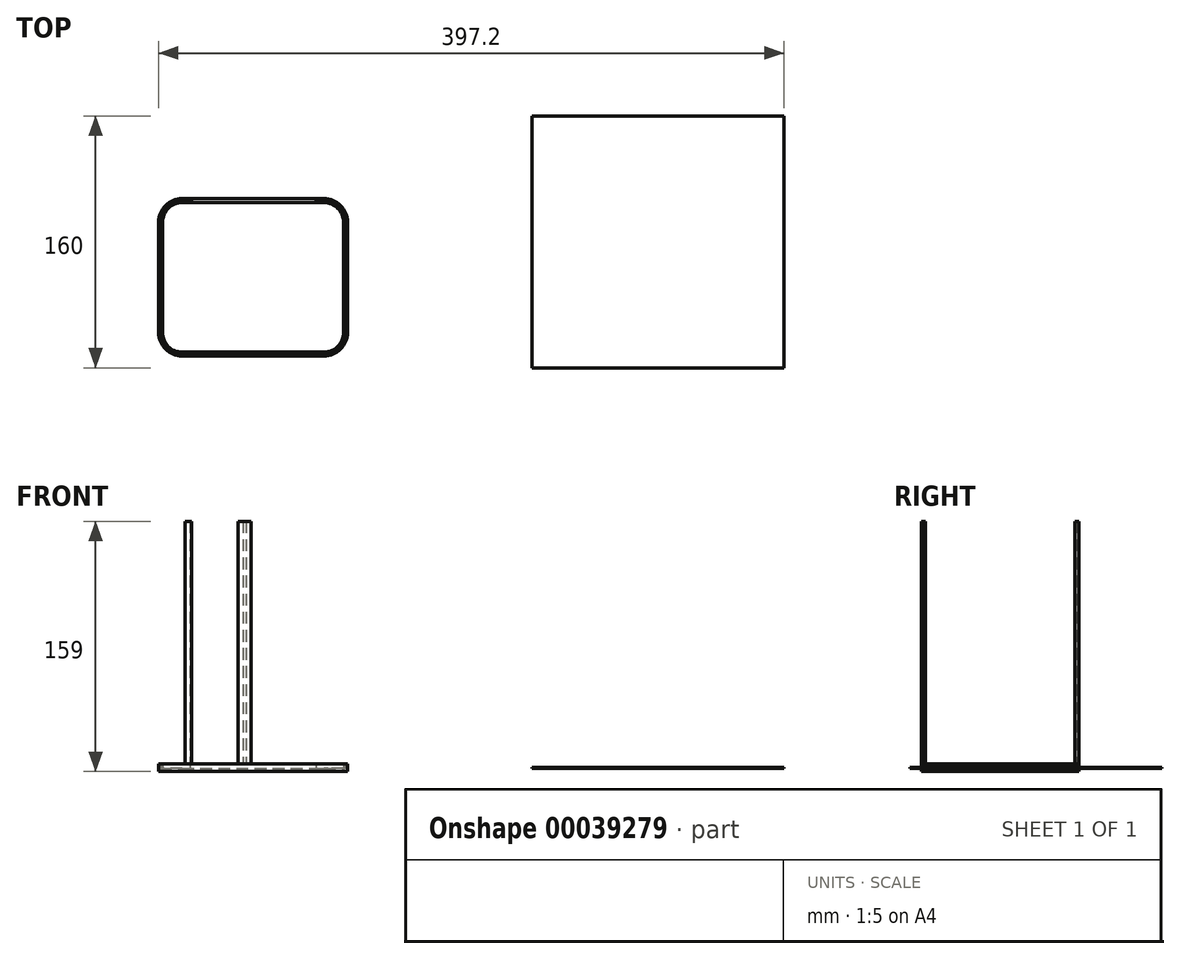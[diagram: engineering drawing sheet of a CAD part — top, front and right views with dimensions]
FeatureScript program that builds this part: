
annotation { "Feature Type Name" : "Feature", "Feature Type Description" : "" }
export const myFeature = defineFeature(function(context is Context, id is Id, definition is map)
    precondition{}
    {
        {
            var Q0;
            Q0=qCreatedBy(makeId("Top.planeOp"),FACE);
            var sketch = newSketch(context, id + "F0", { "sketchPlane" : qUnion([Q0])});
            skLineSegment(sketch, "E0.bottom", {"start": v(0, 0) * mm, "end": v(90, 0) * mm});
            skLineSegment(sketch, "E0.top", {"start": v(0, -100) * mm, "end": v(90, -100) * mm});
            skLineSegment(sketch, "E0.left", {"start": v(-15, -15) * mm, "end": v(-15, -85) * mm});
            skLineSegment(sketch, "E0.right", {"start": v(105, -15) * mm, "end": v(105, -85) * mm});
            skPoint(sketch, "E1.visualSharp", {"position": v(-15, -100) * mm});
            skArc(sketch, "E1.filletArc", {"start": v(-15, -85) * mm, "mid": v(-10.6, -95.6) * mm, "end": v(0, -100) * mm});
            skPoint(sketch, "E2.visualSharp", {"position": v(105, -100) * mm});
            skArc(sketch, "E2.filletArc", {"start": v(90, -100) * mm, "mid": v(100.6, -95.6) * mm, "end": v(105, -85) * mm});
            skPoint(sketch, "E3.visualSharp", {"position": v(105, 0) * mm});
            skArc(sketch, "E3.filletArc", {"start": v(105, -15) * mm, "mid": v(100.6, -4.4) * mm, "end": v(90, 0) * mm});
            skPoint(sketch, "E4.visualSharp", {"position": v(-15, 0) * mm});
            skArc(sketch, "E4.filletArc", {"start": v(0, 0) * mm, "mid": v(-10.6, -4.4) * mm, "end": v(-15, -15) * mm});
            skArc(sketch, "E5.0", {"start": v(0, -2.5) * mm, "mid": v(-8.84, -6.16) * mm, "end": v(-12.5, -15) * mm});
            skLineSegment(sketch, "E5.1", {"start": v(-12.5, -15) * mm, "end": v(-12.5, -85) * mm});
            skLineSegment(sketch, "E5.2", {"start": v(0, -2.5) * mm, "end": v(90, -2.5) * mm});
            skArc(sketch, "E5.3", {"start": v(-12.5, -85) * mm, "mid": v(-8.84, -93.84) * mm, "end": v(0, -97.5) * mm});
            skArc(sketch, "E5.4", {"start": v(102.5, -15) * mm, "mid": v(98.84, -6.16) * mm, "end": v(90, -2.5) * mm});
            skLineSegment(sketch, "E5.5", {"start": v(102.5, -15) * mm, "end": v(102.5, -85) * mm});
            skArc(sketch, "E5.6", {"start": v(90, -97.5) * mm, "mid": v(98.84, -93.84) * mm, "end": v(102.5, -85) * mm});
            skLineSegment(sketch, "E5.7", {"start": v(0, -97.5) * mm, "end": v(90, -97.5) * mm});
            skLineSegment(sketch, "E6.0", {"start": v(0, -0.75) * mm, "end": v(90, -0.75) * mm});
            skArc(sketch, "E6.1", {"start": v(104.25, -15) * mm, "mid": v(100.08, -4.92) * mm, "end": v(90, -0.75) * mm});
            skArc(sketch, "E6.2", {"start": v(0, -0.75) * mm, "mid": v(-10.08, -4.92) * mm, "end": v(-14.25, -15) * mm});
            skLineSegment(sketch, "E6.3", {"start": v(104.25, -15) * mm, "end": v(104.25, -85) * mm});
            skLineSegment(sketch, "E6.4", {"start": v(-14.25, -15) * mm, "end": v(-14.25, -85) * mm});
            skArc(sketch, "E6.5", {"start": v(-14.25, -85) * mm, "mid": v(-10.08, -95.08) * mm, "end": v(0, -99.25) * mm});
            skLineSegment(sketch, "E6.6", {"start": v(0, -99.25) * mm, "end": v(90, -99.25) * mm});
            skArc(sketch, "E6.7", {"start": v(90, -99.25) * mm, "mid": v(100.08, -95.08) * mm, "end": v(104.25, -85) * mm});
            skArc(sketch, "E7.0", {"start": v(0, -1.75) * mm, "mid": v(-9.37, -5.63) * mm, "end": v(-13.25, -15) * mm});
            skLineSegment(sketch, "E7.1", {"start": v(0, -1.75) * mm, "end": v(90, -1.75) * mm});
            skLineSegment(sketch, "E7.2", {"start": v(-13.25, -15) * mm, "end": v(-13.25, -85) * mm});
            skArc(sketch, "E7.3", {"start": v(103.25, -15) * mm, "mid": v(99.37, -5.63) * mm, "end": v(90, -1.75) * mm});
            skArc(sketch, "E7.4", {"start": v(-13.25, -85) * mm, "mid": v(-9.37, -94.37) * mm, "end": v(0, -98.25) * mm});
            skLineSegment(sketch, "E7.5", {"start": v(0, -98.25) * mm, "end": v(90, -98.25) * mm});
            skArc(sketch, "E7.6", {"start": v(90, -98.25) * mm, "mid": v(99.37, -94.37) * mm, "end": v(103.25, -85) * mm});
            skLineSegment(sketch, "E7.7", {"start": v(103.25, -15) * mm, "end": v(103.25, -85) * mm});
            skLineSegment(sketch, "E8", {"start": v(5, 0) * mm, "end": v(5, -2.5) * mm});
            skLineSegment(sketch, "E9", {"start": v(85, 0) * mm, "end": v(85, -2.5) * mm});
            skSolve(sketch);
        }
        {
            var Q0;
            Q0=makeQuery(id+"F0.imprint","IMPRINT",FACE,{"disambiguationData":[TD([[makeQuery(id+"F0.imprint","IMPRINT",EDGE,{"derivedFrom":sQuery(id+"F0.wireOp",EDGE,"E0.top")}),1.0]])]});
            var Q1;
            {var subQ11=sQuery(id+"F0.wireOp",EDGE,"E5.0");Q1=makeQuery(id+"F0.imprint","IMPRINT",FACE,{"disambiguationData":[TD([[makeQuery(id+"F0.imprint","IMPRINT",EDGE,{"derivedFrom":subQ11}),-1.0]])]});}
            var Q2;
            {var subQ3=sQuery(id+"F0.wireOp",EDGE,"E0.bottom");var subQ5=sQuery(id+"F0.wireOp",EDGE,"E8");var subQ7=makeQuery(id+"F0.imprint","INTERSECT",VERTEX,{"derivedFrom":[subQ3,subQ5]});Q2=makeQuery(id+"F0.imprint","IMPRINT",FACE,{"disambiguationData":[TD([[makeQuery(id+"F0.imprint","IMPRINT",EDGE,{"disambiguationData":[TD([[subQ7,-1.0]])],"derivedFrom":subQ3}),-1.0]])]});}
            var Q3;
            {var subQ3=sQuery(id+"F0.wireOp",EDGE,"E6.0");var subQ5=sQuery(id+"F0.wireOp",EDGE,"E8");var subQ7=makeQuery(id+"F0.imprint","INTERSECT",VERTEX,{"derivedFrom":[subQ3,subQ5]});Q3=makeQuery(id+"F0.imprint","IMPRINT",FACE,{"disambiguationData":[TD([[makeQuery(id+"F0.imprint","IMPRINT",EDGE,{"disambiguationData":[TD([[subQ7,-1.0]])],"derivedFrom":subQ3}),-1.0]])]});}
            var Q4;
            {var subQ3=sQuery(id+"F0.wireOp",EDGE,"E8");var subQ5=sQuery(id+"F0.wireOp",EDGE,"E5.2");var subQ7=makeQuery(id+"F0.imprint","INTERSECT",VERTEX,{"derivedFrom":[subQ5,subQ3]});Q4=makeQuery(id+"F0.imprint","IMPRINT",FACE,{"disambiguationData":[TD([[makeQuery(id+"F0.imprint","IMPRINT",EDGE,{"disambiguationData":[TD([[subQ7,-1.0]])],"derivedFrom":subQ5}),1.0]])]});}
            extrude(context, id + "F1", {"entities" : qUnion([Q0, Q1, Q2, Q3, Q4]), "depth" : 3 * mm});
        }
        {
            var Q0;
            Q0=makeQuery(id+"F0.imprint","IMPRINT",FACE,{"disambiguationData":[TD([[makeQuery(id+"F0.imprint","IMPRINT",EDGE,{"derivedFrom":sQuery(id+"F0.wireOp",EDGE,"E0.top")}),1.0]])]});
            var Q1;
            {var subQ3=sQuery(id+"F0.wireOp",EDGE,"E0.bottom");var subQ5=sQuery(id+"F0.wireOp",EDGE,"E8");var subQ7=makeQuery(id+"F0.imprint","INTERSECT",VERTEX,{"derivedFrom":[subQ3,subQ5]});Q1=makeQuery(id+"F0.imprint","IMPRINT",FACE,{"disambiguationData":[TD([[makeQuery(id+"F0.imprint","IMPRINT",EDGE,{"disambiguationData":[TD([[subQ7,-1.0]])],"derivedFrom":subQ3}),-1.0]])]});}
            var Q2;
            {var subQ3=sQuery(id+"F0.wireOp",EDGE,"E5.0");Q2=makeQuery(id+"F0.imprint","IMPRINT",FACE,{"disambiguationData":[TD([[makeQuery(id+"F0.imprint","IMPRINT",EDGE,{"derivedFrom":subQ3}),1.0]])]});}
            var Q3;
            {var subQ11=sQuery(id+"F0.wireOp",EDGE,"E5.0");Q3=makeQuery(id+"F0.imprint","IMPRINT",FACE,{"disambiguationData":[TD([[makeQuery(id+"F0.imprint","IMPRINT",EDGE,{"derivedFrom":subQ11}),-1.0]])]});}
            var Q4;
            {var subQ9=sQuery(id+"F0.wireOp",EDGE,"E6.1");Q4=makeQuery(id+"F0.imprint","IMPRINT",FACE,{"disambiguationData":[TD([[makeQuery(id+"F0.imprint","IMPRINT",EDGE,{"derivedFrom":subQ9}),1.0]])]});}
            var Q5;
            {var subQ3=sQuery(id+"F0.wireOp",EDGE,"E6.0");var subQ5=sQuery(id+"F0.wireOp",EDGE,"E8");var subQ7=makeQuery(id+"F0.imprint","INTERSECT",VERTEX,{"derivedFrom":[subQ3,subQ5]});Q5=makeQuery(id+"F0.imprint","IMPRINT",FACE,{"disambiguationData":[TD([[makeQuery(id+"F0.imprint","IMPRINT",EDGE,{"disambiguationData":[TD([[subQ7,-1.0]])],"derivedFrom":subQ3}),-1.0]])]});}
            var Q6;
            {var subQ3=sQuery(id+"F0.wireOp",EDGE,"E8");var subQ5=sQuery(id+"F0.wireOp",EDGE,"E5.2");var subQ7=makeQuery(id+"F0.imprint","INTERSECT",VERTEX,{"derivedFrom":[subQ5,subQ3]});Q6=makeQuery(id+"F0.imprint","IMPRINT",FACE,{"disambiguationData":[TD([[makeQuery(id+"F0.imprint","IMPRINT",EDGE,{"disambiguationData":[TD([[subQ7,-1.0]])],"derivedFrom":subQ5}),1.0]])]});}
            extrude(context, id + "F2", {"entities" : qUnion([Q0, Q1, Q2, Q3, Q4, Q5, Q6]), "operationType" : NewBodyOperationType.ADD, "oppositeDirection" : true, "depth" : 2 * mm});
        }
        {
            var Q0;
            Q0=qCreatedBy(makeId("Top.planeOp"),FACE);
            var sketch = newSketch(context, id + "F3", { "sketchPlane" : qUnion([Q0])});
            skLineSegment(sketch, "E10.bottom", {"start": v(222.2, 52.57) * mm, "end": v(382.2, 52.57) * mm});
            skLineSegment(sketch, "E10.top", {"start": v(222.2, -107.43) * mm, "end": v(382.2, -107.43) * mm});
            skLineSegment(sketch, "E10.left", {"start": v(222.2, 52.57) * mm, "end": v(222.2, -107.43) * mm});
            skLineSegment(sketch, "E10.right", {"start": v(382.2, 52.57) * mm, "end": v(382.2, -107.43) * mm});
            skSolve(sketch);
        }
        {
            var Q0;
            Q0 = qSketchRegion(id + "F3", true);
            extrude(context, id + "F4", {"entities" : qUnion([Q0]), "depth" : .7 * mm});
        }
        {
            var Q0;
            Q0=makeQuery(id+"F1.opExtrude","CAP_FACE",FACE,{"disambiguationData":[OSD([sQuery(id+"F0.wireOp",EDGE,"E0.bottom"),sQuery(id+"F0.wireOp",EDGE,"E0.top"),sQuery(id+"F0.wireOp",EDGE,"E0.left"),sQuery(id+"F0.wireOp",EDGE,"E0.right"),sQuery(id+"F0.wireOp",EDGE,"E1.filletArc"),sQuery(id+"F0.wireOp",EDGE,"E2.filletArc"),sQuery(id+"F0.wireOp",EDGE,"E3.filletArc"),sQuery(id+"F0.wireOp",EDGE,"E4.filletArc"),sQuery(id+"F0.wireOp",EDGE,"E5.0"),sQuery(id+"F0.wireOp",EDGE,"E5.1"),sQuery(id+"F0.wireOp",EDGE,"E5.2"),sQuery(id+"F0.wireOp",EDGE,"E5.3"),sQuery(id+"F0.wireOp",EDGE,"E5.4"),sQuery(id+"F0.wireOp",EDGE,"E5.5"),sQuery(id+"F0.wireOp",EDGE,"E5.6"),sQuery(id+"F0.wireOp",EDGE,"E5.7"),sQuery(id+"F0.wireOp",EDGE,"E6.0"),sQuery(id+"F0.wireOp",EDGE,"E6.1"),sQuery(id+"F0.wireOp",EDGE,"E6.2"),sQuery(id+"F0.wireOp",EDGE,"E6.3"),sQuery(id+"F0.wireOp",EDGE,"E6.4"),sQuery(id+"F0.wireOp",EDGE,"E6.5"),sQuery(id+"F0.wireOp",EDGE,"E6.6"),sQuery(id+"F0.wireOp",EDGE,"E6.7"),sQuery(id+"F0.wireOp",EDGE,"E7.0"),sQuery(id+"F0.wireOp",EDGE,"E7.1"),sQuery(id+"F0.wireOp",EDGE,"E7.2"),sQuery(id+"F0.wireOp",EDGE,"E7.3"),sQuery(id+"F0.wireOp",EDGE,"E7.4"),sQuery(id+"F0.wireOp",EDGE,"E7.5"),sQuery(id+"F0.wireOp",EDGE,"E7.6"),sQuery(id+"F0.wireOp",EDGE,"E7.7"),sQuery(id+"F0.wireOp",EDGE,"E8"),sQuery(id+"F0.wireOp",EDGE,"E9")])],"isStart":false});
            var sketch = newSketch(context, id + "F5", { "sketchPlane" : qUnion([Q0])});
            skLineSegment(sketch, "E11", {"start": v(2, 0) * mm, "end": v(2, -0.75) * mm});
            skLineSegment(sketch, "E12", {"start": v(2, 0) * mm, "end": v(6, 0) * mm});
            skLineSegment(sketch, "E13", {"start": v(6, 0) * mm, "end": v(6, -2.5) * mm});
            skLineSegment(sketch, "E14", {"start": v(6, -2.5) * mm, "end": v(2, -2.5) * mm});
            skLineSegment(sketch, "E15", {"start": v(2, -0.75) * mm, "end": v(5, -0.75) * mm});
            skLineSegment(sketch, "E16", {"start": v(5, -0.75) * mm, "end": v(5, -1.75) * mm});
            skLineSegment(sketch, "E17", {"start": v(5, -1.75) * mm, "end": v(2, -1.75) * mm});
            skLineSegment(sketch, "E18.trimOffspring", {"start": v(2, -1.75) * mm, "end": v(2, -2.5) * mm});
            skLineSegment(sketch, "E19.bottom", {"start": v(35.66, -97.5) * mm, "end": v(43.66, -97.5) * mm});
            skLineSegment(sketch, "E19.top", {"start": v(35.66, -100) * mm, "end": v(43.66, -100) * mm});
            skLineSegment(sketch, "E19.left", {"start": v(35.66, -97.5) * mm, "end": v(35.66, -98.25) * mm});
            skLineSegment(sketch, "E19.right", {"start": v(43.66, -97.5) * mm, "end": v(43.66, -98.25) * mm});
            skLineSegment(sketch, "E20.bottom", {"start": v(35.66, -98.25) * mm, "end": v(38.66, -98.25) * mm});
            skLineSegment(sketch, "E20.top", {"start": v(35.66, -99.25) * mm, "end": v(38.66, -99.25) * mm});
            skLineSegment(sketch, "E21.bottom", {"start": v(43.66, -98.25) * mm, "end": v(40.66, -98.25) * mm});
            skLineSegment(sketch, "E21.top", {"start": v(43.66, -99.25) * mm, "end": v(40.66, -99.25) * mm});
            skLineSegment(sketch, "E22.trimOffspring", {"start": v(35.66, -99.25) * mm, "end": v(35.66, -100) * mm});
            skLineSegment(sketch, "E23.trimOffspring", {"start": v(43.66, -99.25) * mm, "end": v(43.66, -100) * mm});
            skLineSegment(sketch, "E24", {"start": v(35.66, -97.5) * mm, "end": v(0, -97.5) * mm, "construction": true});
            skLineSegment(sketch, "E25", {"start": v(43.66, -97.5) * mm, "end": v(90, -97.5) * mm, "construction": true});
            skLineSegment(sketch, "E26", {"start": v(90, -97.5) * mm, "end": v(43.66, -97.5) * mm, "construction": true});
            skLineSegment(sketch, "E27", {"start": v(38.66, -98.25) * mm, "end": v(38.66, -99.25) * mm});
            skLineSegment(sketch, "E28", {"start": v(40.66, -98.25) * mm, "end": v(40.66, -99.25) * mm});
            skSolve(sketch);
        }
        {
            var Q0;
            Q0 = qSketchRegion(id + "F5", true);
            extrude(context, id + "F6", {"entities" : qUnion([Q0]), "depth" : 154 * mm});
        }
    });
